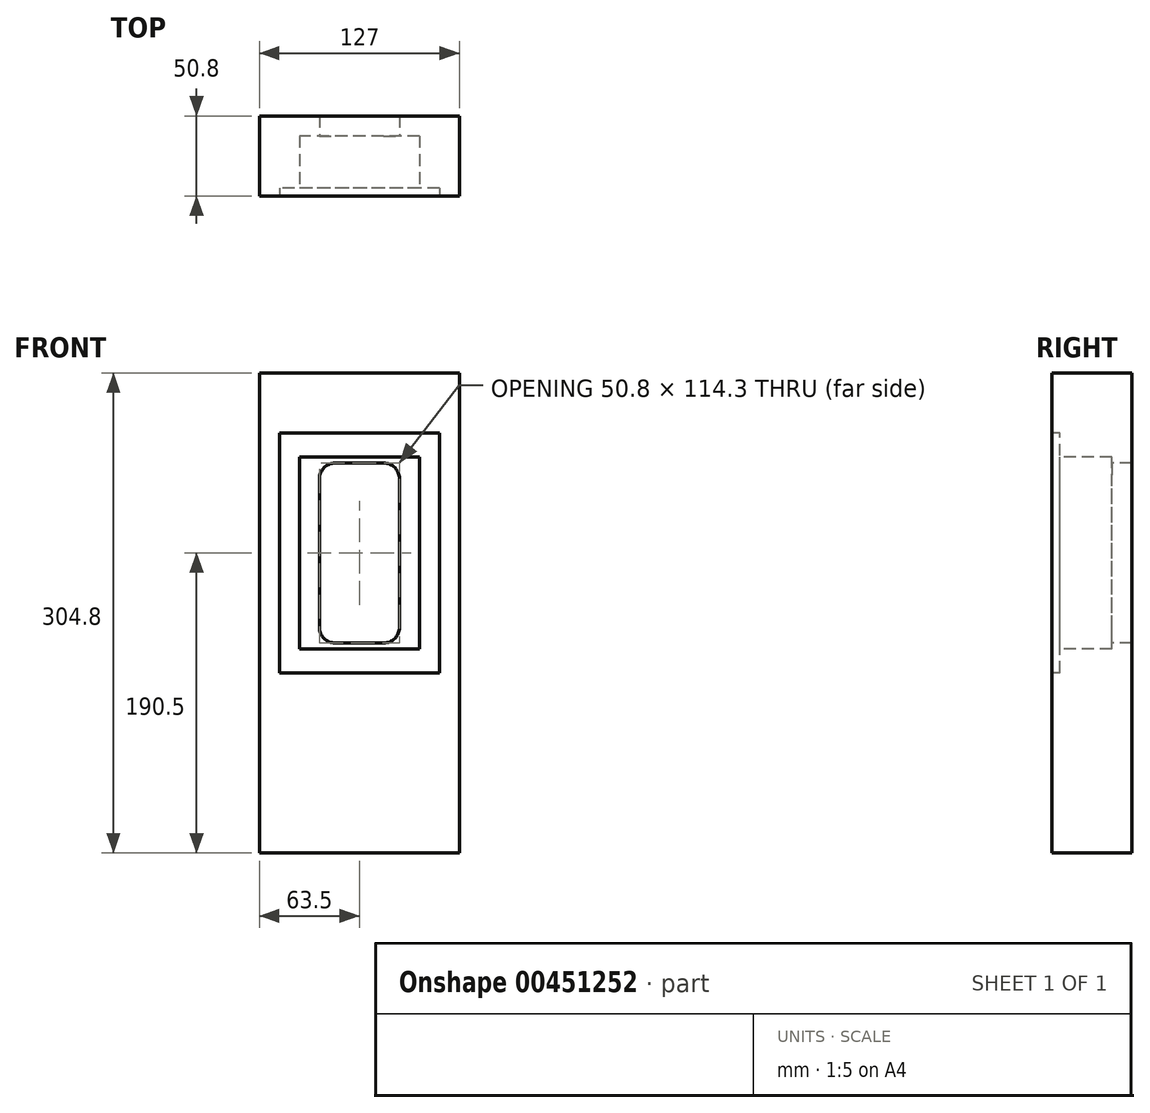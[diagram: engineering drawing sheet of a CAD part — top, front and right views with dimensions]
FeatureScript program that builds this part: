
annotation { "Feature Type Name" : "Feature", "Feature Type Description" : "" }
export const myFeature = defineFeature(function(context is Context, id is Id, definition is map)
    precondition{}
    {
        {
            var Q0;
            Q0=qCreatedBy(makeId("Front.planeOp"),FACE);
            var sketch = newSketch(context, id + "F0", { "sketchPlane" : qUnion([Q0])});
            skLineSegment(sketch, "E0.top", {"start": v(63.5, 114.3) * mm, "end": v(-63.5, 114.3) * mm});
            skLineSegment(sketch, "E0.left", {"start": v(63.5, -190.5) * mm, "end": v(63.5, 114.3) * mm});
            skLineSegment(sketch, "E0.right", {"start": v(-63.5, -190.5) * mm, "end": v(-63.5, 114.3) * mm});
            skPoint(sketch, "E0.middle", {"position": v(0, 0) * mm});
            skLineSegment(sketch, "E1.bottom", {"start": v(50.8, -76.2) * mm, "end": v(-50.8, -76.2) * mm});
            skLineSegment(sketch, "E1.top", {"start": v(50.8, 76.2) * mm, "end": v(-50.8, 76.2) * mm});
            skLineSegment(sketch, "E1.left", {"start": v(50.8, -76.2) * mm, "end": v(50.8, 76.2) * mm});
            skLineSegment(sketch, "E1.right", {"start": v(-50.8, -76.2) * mm, "end": v(-50.8, 76.2) * mm});
            skLineSegment(sketch, "E2.bottom", {"start": v(38.1, -60.96) * mm, "end": v(-38.1, -60.96) * mm});
            skLineSegment(sketch, "E2.top", {"start": v(38.1, 60.96) * mm, "end": v(-38.1, 60.96) * mm});
            skLineSegment(sketch, "E2.left", {"start": v(38.1, -60.96) * mm, "end": v(38.1, 60.96) * mm});
            skLineSegment(sketch, "E2.right", {"start": v(-38.1, -60.96) * mm, "end": v(-38.1, 60.96) * mm});
            skLineSegment(sketch, "E3.bottom", {"start": v(25.4, -57.15) * mm, "end": v(-25.4, -57.15) * mm});
            skLineSegment(sketch, "E3.top", {"start": v(25.4, 57.15) * mm, "end": v(-25.4, 57.15) * mm});
            skLineSegment(sketch, "E3.left", {"start": v(25.4, -57.15) * mm, "end": v(25.4, 57.15) * mm});
            skLineSegment(sketch, "E3.right", {"start": v(-25.4, -57.15) * mm, "end": v(-25.4, 57.15) * mm});
            skLineSegment(sketch, "E4", {"start": v(-63.5, -190.5) * mm, "end": v(63.5, -190.5) * mm});
            skPoint(sketch, "E5.orphan", {"position": v(-63.5, -114.3) * mm});
            skPoint(sketch, "E6.orphan", {"position": v(63.5, -114.3) * mm});
            skSolve(sketch);
        }
        {
            var Q0;
            Q0=makeQuery(id+"F0.imprint","IMPRINT",FACE,{"disambiguationData":[TD([[makeQuery(id+"F0.imprint","IMPRINT",EDGE,{"derivedFrom":sQuery(id+"F0.wireOp",EDGE,"E0.top")}),1.0]])]});
            var Q1;
            Q1=makeQuery(id+"F0.imprint","IMPRINT",FACE,{"disambiguationData":[TD([[makeQuery(id+"F0.imprint","IMPRINT",EDGE,{"derivedFrom":sQuery(id+"F0.wireOp",EDGE,"E1.bottom")}),-1.0]])]});
            var Q2;
            Q2=makeQuery(id+"F0.imprint","IMPRINT",FACE,{"disambiguationData":[TD([[makeQuery(id+"F0.imprint","IMPRINT",EDGE,{"derivedFrom":sQuery(id+"F0.wireOp",EDGE,"E2.bottom")}),-1.0]])]});
            extrude(context, id + "F1", {"entities" : qUnion([Q0, Q1, Q2]), "oppositeDirection" : true, "depth" : 50.8 * mm});
        }
        {
            var Q0;
            Q0=makeQuery(id+"F0.imprint","IMPRINT",FACE,{"disambiguationData":[TD([[makeQuery(id+"F0.imprint","IMPRINT",EDGE,{"derivedFrom":sQuery(id+"F0.wireOp",EDGE,"E1.bottom")}),-1.0]])]});
            extrude(context, id + "F2", {"entities" : qUnion([Q0]), "operationType" : NewBodyOperationType.REMOVE, "oppositeDirection" : true, "depth" : 5 * mm});
        }
        {
            var Q0;
            Q0=makeQuery(id+"F0.imprint","IMPRINT",FACE,{"disambiguationData":[TD([[makeQuery(id+"F0.imprint","IMPRINT",EDGE,{"derivedFrom":sQuery(id+"F0.wireOp",EDGE,"E2.bottom")}),-1.0]])]});
            extrude(context, id + "F3", {"entities" : qUnion([Q0]), "operationType" : NewBodyOperationType.REMOVE, "oppositeDirection" : true, "depth" : 38.1 * mm});
        }
        {
            var Q0;
            Q0=makeQuery(id+"F1.opExtrude","SWEPT_EDGE",EDGE,{"disambiguationData":[OSD([sQuery(id+"F0.wireOp",EDGE,"E3.top"),sQuery(id+"F0.wireOp",EDGE,"E3.right")])]});
            var Q1;
            Q1=makeQuery(id+"F1.opExtrude","SWEPT_EDGE",EDGE,{"disambiguationData":[OSD([sQuery(id+"F0.wireOp",EDGE,"E3.top"),sQuery(id+"F0.wireOp",EDGE,"E3.left")])]});
            var Q2;
            Q2=makeQuery(id+"F1.opExtrude","SWEPT_EDGE",EDGE,{"disambiguationData":[OSD([sQuery(id+"F0.wireOp",EDGE,"E3.bottom"),sQuery(id+"F0.wireOp",EDGE,"E3.right")])]});
            var Q3;
            Q3=makeQuery(id+"F1.opExtrude","SWEPT_EDGE",EDGE,{"disambiguationData":[OSD([sQuery(id+"F0.wireOp",EDGE,"E3.bottom"),sQuery(id+"F0.wireOp",EDGE,"E3.left")])]});
            fillet(context, id + "F4", {"entities" : qUnion([Q0, Q1, Q2, Q3]), "radius" : 10 * mm, "tangentPropagation" : true, "allowEdgeOverflow" : false});
        }
    });
